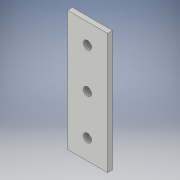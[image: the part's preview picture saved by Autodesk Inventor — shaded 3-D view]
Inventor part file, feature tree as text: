
AUTODESK INVENTOR PART (.ipt)
format: ipt  version: 2018 (Build 220112000, 112)  size: 102,912 bytes
history: native  units: in
note: dims shown in document units (in); Inventor stores cm internally (conversion verified against a paired STEP export)
features: extrude x1, sketch x1
ambient origin geometry x8: Origin, YZ Plane, XZ Plane, XY Plane, X Axis, Y Axis, Z Axis, Center Point
bodies: Solid1 (feature_tree)
feature tree (2):
  extrude  "Extrusion1"  Depth=3.0in
  sketch  "Sketch1"  dims[d0=1.0in d1=3.0in d2=0.5in d3=1.0in d4=1.0in d5=0.2031in d6=0.125in d7=0.0in]
